# Revit family: FBVKZ22T
name_source: partatom
category: Allgemeines Modell
units: mm (PartAtom-declared; Revit-internal decimal feet)

## family parameters
Arbeitsebenenbasiert = Nein
Beim Laden mit Abzugskörper schneiden = Nein
Bemaßung runder Anschluss = Durchmesser verwenden
Beschriftungsausrichtung beibehalten = Nein
Gemeinsam genutzt = Nein
Immer vertikal = Ja
Kann Basisbauteil für Bewehrung sein = Nein
Raumberechnungspunkt = Nein
Teiletyp = Normal

## types (1)
- FBVKZ22T
    Bauteilnummer = FBVKZ22T
    DocNumber = FBVKZ22T.ipt
    Erstellungsdatum = 14.01.2019
    Folder = ARTIKEL\G1_Abstandhalter\G1C_Mauerstärke\FBVK%\
    Genehmigungsdatum Konstr. = 08.12.2021
    Gewicht = 0.069
    Kennung = Artikel
    Konstruktionsstatus = 1
    Revisionsnummer = -
    Status = In Bearbeitung
    VDS_Category = 3D-Konstruktion Bauteil
    Vorgabe-Ansicht = 0 mm  [stored 0 ft]
    d10 = 21 mm
    d11 = 23 mm
    d12 = 33 mm  [stored 0.108268 ft]
    d15 = 6 mm  [stored 0.019685 ft]
    d8 = 40 mm  [stored 0.131234 ft]
    d9 = 43 mm

note: [stored X ft] marks values corroborated as IEEE doubles in the binary element streams (Revit-internal decimal feet)
